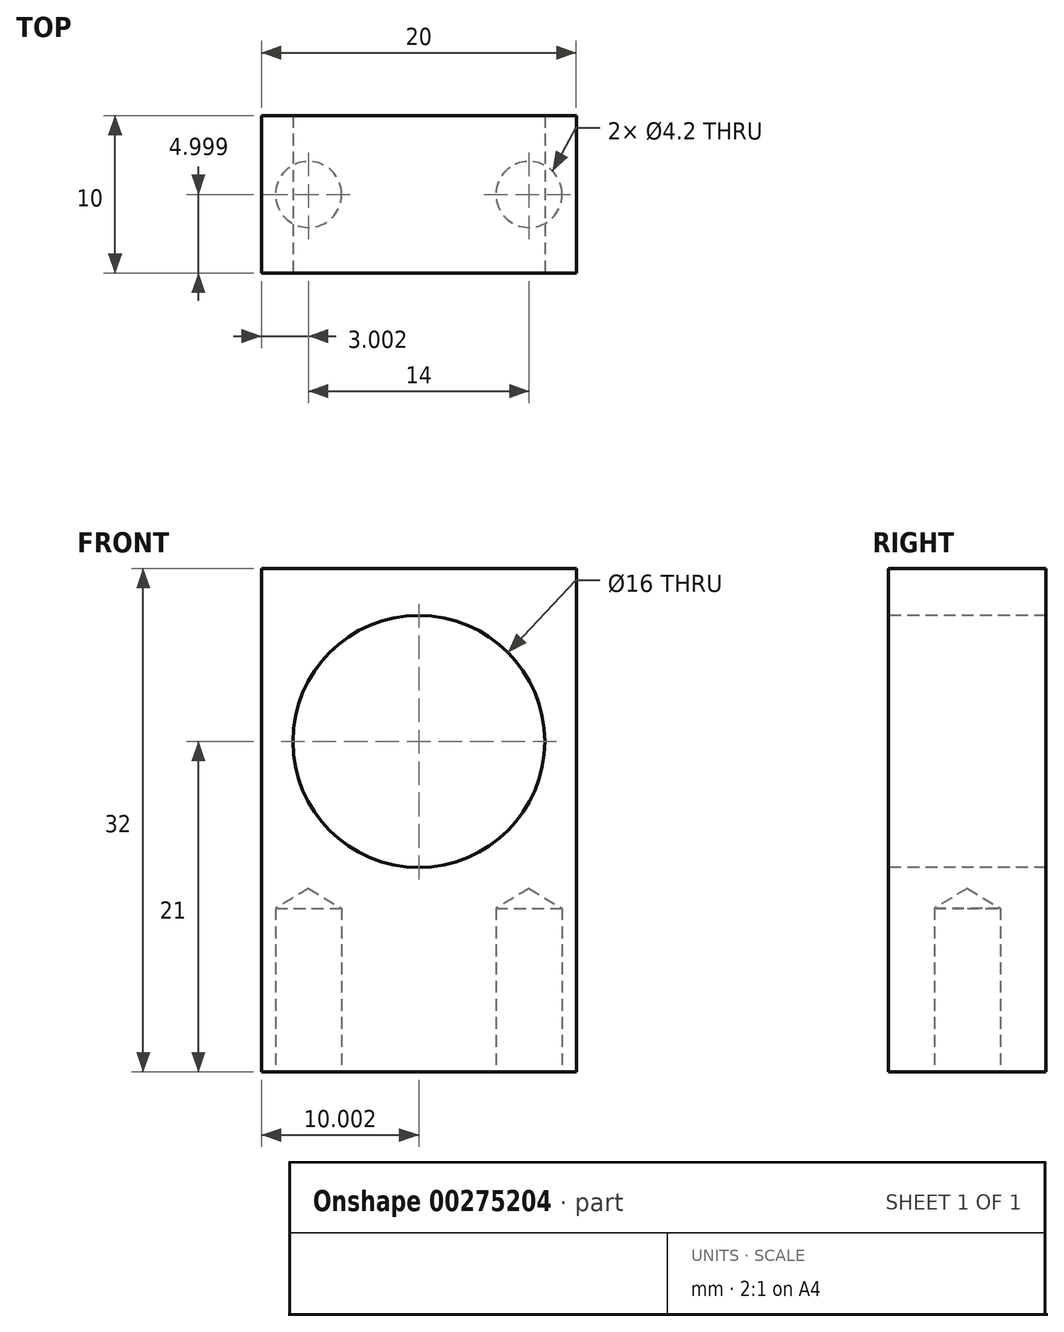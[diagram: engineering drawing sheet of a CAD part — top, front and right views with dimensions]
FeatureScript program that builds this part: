
annotation { "Feature Type Name" : "Feature", "Feature Type Description" : "" }
export const myFeature = defineFeature(function(context is Context, id is Id, definition is map)
    precondition{}
    {
        {
            var Q0;
            Q0=qCreatedBy(makeId("Top.planeOp"),FACE);
            var sketch = newSketch(context, id + "F0", { "sketchPlane" : qUnion([Q0])});
            skLineSegment(sketch, "E0.bottom", {"start": v(-37.62, 18.06) * mm, "end": v(-17.62, 18.06) * mm});
            skLineSegment(sketch, "E0.top", {"start": v(-37.62, 8.06) * mm, "end": v(-17.62, 8.06) * mm});
            skLineSegment(sketch, "E0.left", {"start": v(-37.62, 18.06) * mm, "end": v(-37.62, 8.06) * mm});
            skLineSegment(sketch, "E0.right", {"start": v(-17.62, 18.06) * mm, "end": v(-17.62, 8.06) * mm});
            skSolve(sketch);
        }
        {
            var Q0;
            Q0=makeQuery(id+"F0.imprint","IMPRINT",FACE,{"disambiguationData":[TD([[makeQuery(id+"F0.imprint","IMPRINT",EDGE,{"derivedFrom":sQuery(id+"F0.wireOp",EDGE,"E0.bottom")}),-1.0]])]});
            extrude(context, id + "F1", {"entities" : qUnion([Q0]), "depth" : 32 * mm});
        }
        {
            var Q0;
            Q0=makeQuery(id+"F1.opExtrude","SWEPT_FACE",FACE,{"disambiguationData":[OSD([sQuery(id+"F0.wireOp",EDGE,"E0.top")])]});
            var sketch = newSketch(context, id + "F2", { "sketchPlane" : qUnion([Q0])});
            skLineSegment(sketch, "E1", {"start": v(-37.62, 21) * mm, "end": v(-17.62, 21) * mm, "construction": true});
            skCircle(sketch, "E2", {"center": v(-27.62, 21) * mm, "radius": 8 * mm});
            skSolve(sketch);
        }
        {
            var Q0;
            Q0=makeQuery(id+"F2.imprint","IMPRINT",FACE,{"disambiguationData":[TD([[makeQuery(id+"F2.imprint","IMPRINT",EDGE,{"derivedFrom":sQuery(id+"F2.wireOp",EDGE,"E2")}),1.0]])]});
            extrude(context, id + "F3", {"entities" : qUnion([Q0]), "operationType" : NewBodyOperationType.REMOVE, "oppositeDirection" : true, "depth" : 25 * mm});
        }
        {
            var Q0;
            Q0=makeQuery(id+"F1.opExtrude","CAP_FACE",FACE,{"disambiguationData":[OSD([sQuery(id+"F0.wireOp",EDGE,"E0.bottom"),sQuery(id+"F0.wireOp",EDGE,"E0.top"),sQuery(id+"F0.wireOp",EDGE,"E0.left"),sQuery(id+"F0.wireOp",EDGE,"E0.right")])],"isStart":true});
            var sketch = newSketch(context, id + "F4", { "sketchPlane" : qUnion([Q0])});
            skLineSegment(sketch, "E3", {"start": v(-27.62, -8.06) * mm, "end": v(-27.62, -18.06) * mm, "construction": true});
            skLineSegment(sketch, "E4", {"start": v(-37.62, -13.06) * mm, "end": v(-17.62, -13.06) * mm, "construction": true});
            skPoint(sketch, "E5", {"position": v(-34.62, -13.06) * mm});
            skPoint(sketch, "E6", {"position": v(-20.62, -13.06) * mm});
            skSolve(sketch);
        }
        {
            var Q0;
            Q0=sQuery(id+"F4.wireOp",VERTEX,"E5");
            var Q1;
            Q1=sQuery(id+"F4.wireOp",VERTEX,"E6");
            var Q2;
            Q2=makeQuery(id+"F1.opExtrude","SWEPT_BODY",BODY,{"disambiguationData":[OSD([sQuery(id+"F0.wireOp",EDGE,"E0.bottom"),sQuery(id+"F0.wireOp",EDGE,"E0.top"),sQuery(id+"F0.wireOp",EDGE,"E0.left"),sQuery(id+"F0.wireOp",EDGE,"E0.right")])]});
            hole(context, id + "F5", {"style" : HoleStyle.SIMPLE, "endStyle" : HoleEndStyle.BLIND, "standardTappedOrClearance" : lookupTablePath({ "standard" : "ISO", "engagement" : "75%", "pitch" : "0.8 mm", "size" : "M5", "type" : "Tapped" }), "standardBlindInLast" : lookupTablePath({ "standard" : "ISO", "engagement" : "75%", "pitch" : "0.8 mm", "size" : "M5", "type" : "Tapped" }), "holeDiameter" : 4.2 * mm, "showTappedDepth" : true, "holeDepth" : 10.4 * mm, "isTappedThrough" : true, "tappedDepth" : 8 * mm, "tapClearance" : 3, "startFromSketch" : true, "locations" : qUnion([Q0, Q1]), "scope" : qUnion([Q2]), "majorDiameter" : 5 * mm});
        }
    });
